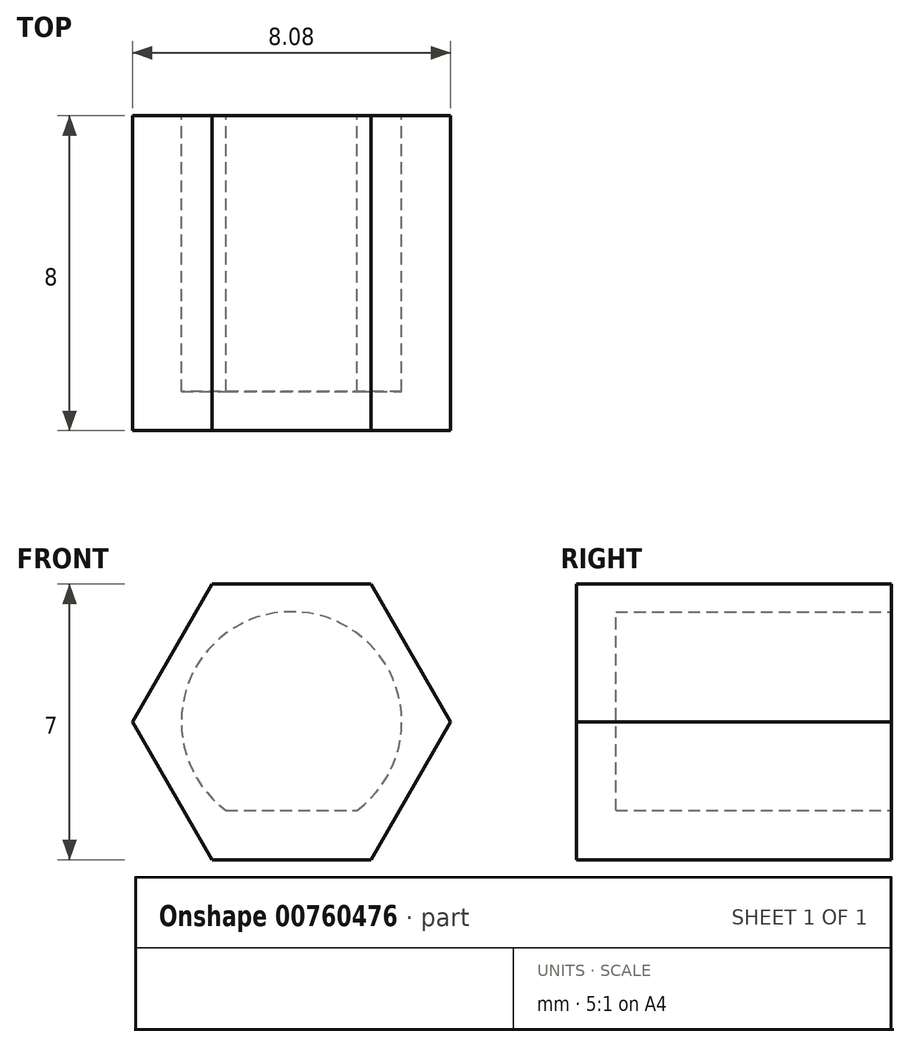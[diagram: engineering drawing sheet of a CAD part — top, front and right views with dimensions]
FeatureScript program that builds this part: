
annotation { "Feature Type Name" : "Feature", "Feature Type Description" : "" }
export const myFeature = defineFeature(function(context is Context, id is Id, definition is map)
    precondition{}
    {
        {
            var Q0;
            Q0=qCreatedBy(makeId("Front.planeOp"),FACE);
            var sketch = newSketch(context, id + "F0", { "sketchPlane" : qUnion([Q0])});
            skCircle(sketch, "E0", {"center": v(0, 0) * mm, "radius": 2.8 * mm});
            skCircle(sketch, "E1.cCircle", {"center": v(0, 0) * mm, "radius": 3.5 * mm, "construction": true});
            skLineSegment(sketch, "E1.0", {"start": v(-2.02, 3.5) * mm, "end": v(2.02, 3.5) * mm});
            skLineSegment(sketch, "E1.1", {"start": v(2.02, 3.5) * mm, "end": v(4.04, 0) * mm});
            skLineSegment(sketch, "E1.2", {"start": v(4.04, 0) * mm, "end": v(2.02, -3.5) * mm});
            skLineSegment(sketch, "E1.3", {"start": v(2.02, -3.5) * mm, "end": v(-2.02, -3.5) * mm});
            skLineSegment(sketch, "E1.4", {"start": v(-2.02, -3.5) * mm, "end": v(-4.04, 0) * mm});
            skLineSegment(sketch, "E1.5", {"start": v(-4.04, 0) * mm, "end": v(-2.02, 3.5) * mm});
            skPoint(sketch, "E1.0.midPoint", {"position": v(0, 3.5) * mm});
            skLineSegment(sketch, "E2", {"start": v(-1.67, -2.25) * mm, "end": v(1.67, -2.25) * mm});
            skSolve(sketch);
        }
        {
            var Q0;
            Q0=makeQuery(id+"F0.imprint","IMPRINT",FACE,{"disambiguationData":[TD([[makeQuery(id+"F0.imprint","IMPRINT",EDGE,{"derivedFrom":sQuery(id+"F0.wireOp",EDGE,"E1.0")}),-1.0]])]});
            var Q1;
            {var subQ0=sQuery(id+"F0.wireOp",EDGE,"E2");Q1=makeQuery(id+"F0.imprint","IMPRINT",FACE,{"disambiguationData":[TD([[makeQuery(id+"F0.imprint","IMPRINT",EDGE,{"derivedFrom":subQ0}),1.0]])]});}
            var Q2;
            {var subQ0=sQuery(id+"F0.wireOp",EDGE,"E2");Q2=makeQuery(id+"F0.imprint","IMPRINT",FACE,{"disambiguationData":[TD([[makeQuery(id+"F0.imprint","IMPRINT",EDGE,{"derivedFrom":subQ0}),-1.0]])]});}
            extrude(context, id + "F1", {"entities" : qUnion([Q0, Q1, Q2]), "depth" : 8 * mm, "offsetDistance" : 25 * mm});
        }
        {
            var Q0;
            {var subQ0=sQuery(id+"F0.wireOp",EDGE,"E2");Q0=makeQuery(id+"F0.imprint","IMPRINT",FACE,{"disambiguationData":[TD([[makeQuery(id+"F0.imprint","IMPRINT",EDGE,{"derivedFrom":subQ0}),1.0]])]});}
            extrude(context, id + "F2", {"entities" : qUnion([Q0]), "operationType" : NewBodyOperationType.REMOVE, "depth" : 7 * mm, "offsetDistance" : 25 * mm});
        }
    });
